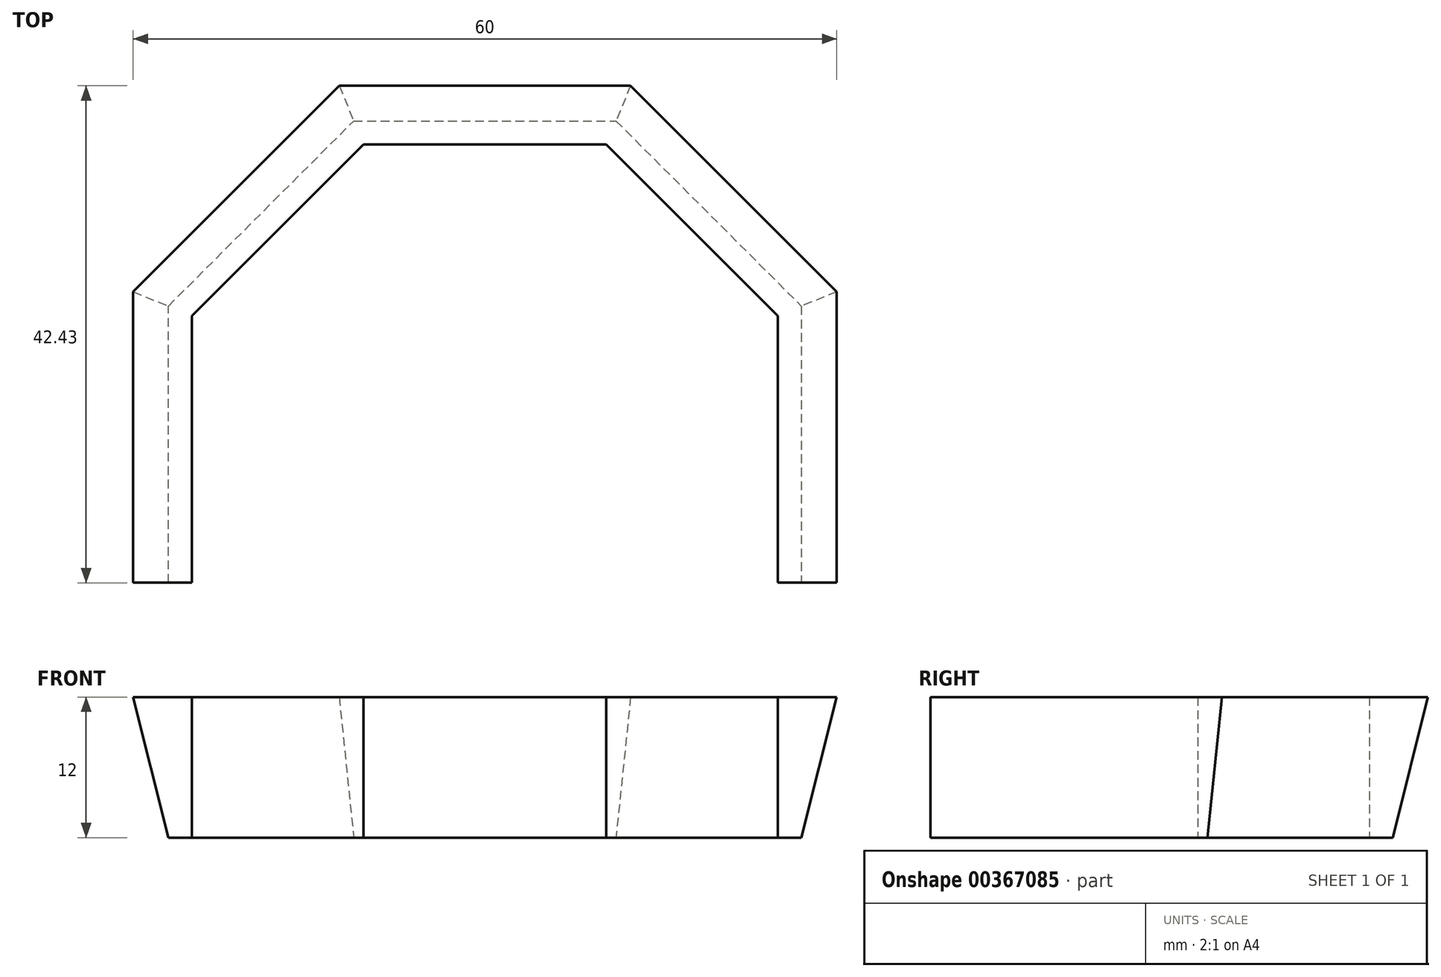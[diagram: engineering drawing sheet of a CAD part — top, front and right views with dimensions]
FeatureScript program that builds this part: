
annotation { "Feature Type Name" : "Feature", "Feature Type Description" : "" }
export const myFeature = defineFeature(function(context is Context, id is Id, definition is map)
    precondition{}
    {
        {
            var Q0;
            Q0=qCreatedBy(makeId("Top.planeOp"),FACE);
            var sketch = newSketch(context, id + "F0", { "sketchPlane" : qUnion([Q0])});
            skCircle(sketch, "E0.cCircle", {"center": v(0, 0) * mm, "radius": 30 * mm, "construction": true});
            skLineSegment(sketch, "E0.0", {"start": v(-12.43, 30) * mm, "end": v(12.43, 30) * mm});
            skLineSegment(sketch, "E0.1", {"start": v(12.43, 30) * mm, "end": v(30, 12.43) * mm});
            skLineSegment(sketch, "E0.2", {"start": v(30, 12.43) * mm, "end": v(30, -12.43) * mm});
            skLineSegment(sketch, "E0.3", {"start": v(30, -12.43) * mm, "end": v(12.43, -30) * mm, "construction": true});
            skLineSegment(sketch, "E0.4", {"start": v(12.43, -30) * mm, "end": v(-12.43, -30) * mm, "construction": true});
            skLineSegment(sketch, "E0.5", {"start": v(-12.43, -30) * mm, "end": v(-30, -12.43) * mm, "construction": true});
            skLineSegment(sketch, "E0.6", {"start": v(-30, -12.43) * mm, "end": v(-30, 12.43) * mm});
            skLineSegment(sketch, "E0.7", {"start": v(-30, 12.43) * mm, "end": v(-12.43, 30) * mm});
            skPoint(sketch, "E0.0.midPoint", {"position": v(0, 30) * mm});
            skCircle(sketch, "E1.cCircle", {"center": v(0, 0) * mm, "radius": 40 * mm, "construction": true});
            skLineSegment(sketch, "E1.0", {"start": v(-16.57, 40) * mm, "end": v(16.57, 40) * mm, "construction": true});
            skLineSegment(sketch, "E1.1", {"start": v(16.57, 40) * mm, "end": v(40, 16.57) * mm, "construction": true});
            skLineSegment(sketch, "E1.2", {"start": v(40, 16.57) * mm, "end": v(40, -16.57) * mm, "construction": true});
            skLineSegment(sketch, "E1.3", {"start": v(40, -16.57) * mm, "end": v(16.57, -40) * mm, "construction": true});
            skLineSegment(sketch, "E1.4", {"start": v(16.57, -40) * mm, "end": v(-16.57, -40) * mm, "construction": true});
            skLineSegment(sketch, "E1.5", {"start": v(-16.57, -40) * mm, "end": v(-40, -16.57) * mm, "construction": true});
            skLineSegment(sketch, "E1.6", {"start": v(-40, -16.57) * mm, "end": v(-40, 16.57) * mm, "construction": true});
            skLineSegment(sketch, "E1.7", {"start": v(-40, 16.57) * mm, "end": v(-16.57, 40) * mm, "construction": true});
            skPoint(sketch, "E1.0.midPoint", {"position": v(0, 40) * mm});
            skLineSegment(sketch, "E2", {"start": v(-30, -12.43) * mm, "end": v(-25, -12.43) * mm});
            skLineSegment(sketch, "E3", {"start": v(-25, -12.43) * mm, "end": v(-25, 10.36) * mm});
            skLineSegment(sketch, "E4", {"start": v(-25, 10.36) * mm, "end": v(-10.36, 25) * mm});
            skLineSegment(sketch, "E5", {"start": v(-10.36, 25) * mm, "end": v(10.36, 25) * mm});
            skLineSegment(sketch, "E6", {"start": v(10.36, 25) * mm, "end": v(25, 10.36) * mm});
            skLineSegment(sketch, "E7", {"start": v(25, 10.36) * mm, "end": v(25, -12.43) * mm});
            skLineSegment(sketch, "E8", {"start": v(25, -12.43) * mm, "end": v(30, -12.43) * mm});
            skLineSegment(sketch, "E9", {"start": v(-17.68, 17.68) * mm, "end": v(-21.21, 21.21) * mm, "construction": true});
            skPoint(sketch, "E9.endSnap0", {"position": v(-21.21, 21.21) * mm});
            skLineSegment(sketch, "E10", {"start": v(0, 25) * mm, "end": v(0, 30) * mm, "construction": true});
            skSolve(sketch);
        }
        {
            var Q0;
            Q0 = qSketchRegion(id + "F0", true);
            extrude(context, id + "F1", {"entities" : qUnion([Q0]), "depth" : 12 * mm});
        }
        {
            var Q0;
            Q0=makeQuery(id+"F1.opExtrude","CAP_EDGE",EDGE,{"disambiguationData":[OSD([sQuery(id+"F0.wireOp",EDGE,"E0.6")])],"isStart":true});
            var Q1;
            Q1=makeQuery(id+"F1.opExtrude","CAP_EDGE",EDGE,{"disambiguationData":[OSD([sQuery(id+"F0.wireOp",EDGE,"E0.7")])],"isStart":true});
            var Q2;
            Q2=makeQuery(id+"F1.opExtrude","CAP_EDGE",EDGE,{"disambiguationData":[OSD([sQuery(id+"F0.wireOp",EDGE,"E0.0")])],"isStart":true});
            var Q3;
            Q3=makeQuery(id+"F1.opExtrude","CAP_EDGE",EDGE,{"disambiguationData":[OSD([sQuery(id+"F0.wireOp",EDGE,"E0.1")])],"isStart":true});
            var Q4;
            Q4=makeQuery(id+"F1.opExtrude","CAP_EDGE",EDGE,{"disambiguationData":[OSD([sQuery(id+"F0.wireOp",EDGE,"E0.2")])],"isStart":true});
            chamfer(context, id + "F2", {"entities" : qUnion([Q0, Q1, Q2, Q3, Q4]), "chamferType" : ChamferType.TWO_OFFSETS, "width1" : 3 * mm, "oppositeDirection" : false, "width2" : 12 * mm, "tangentPropagation" : true});
        }
    });
